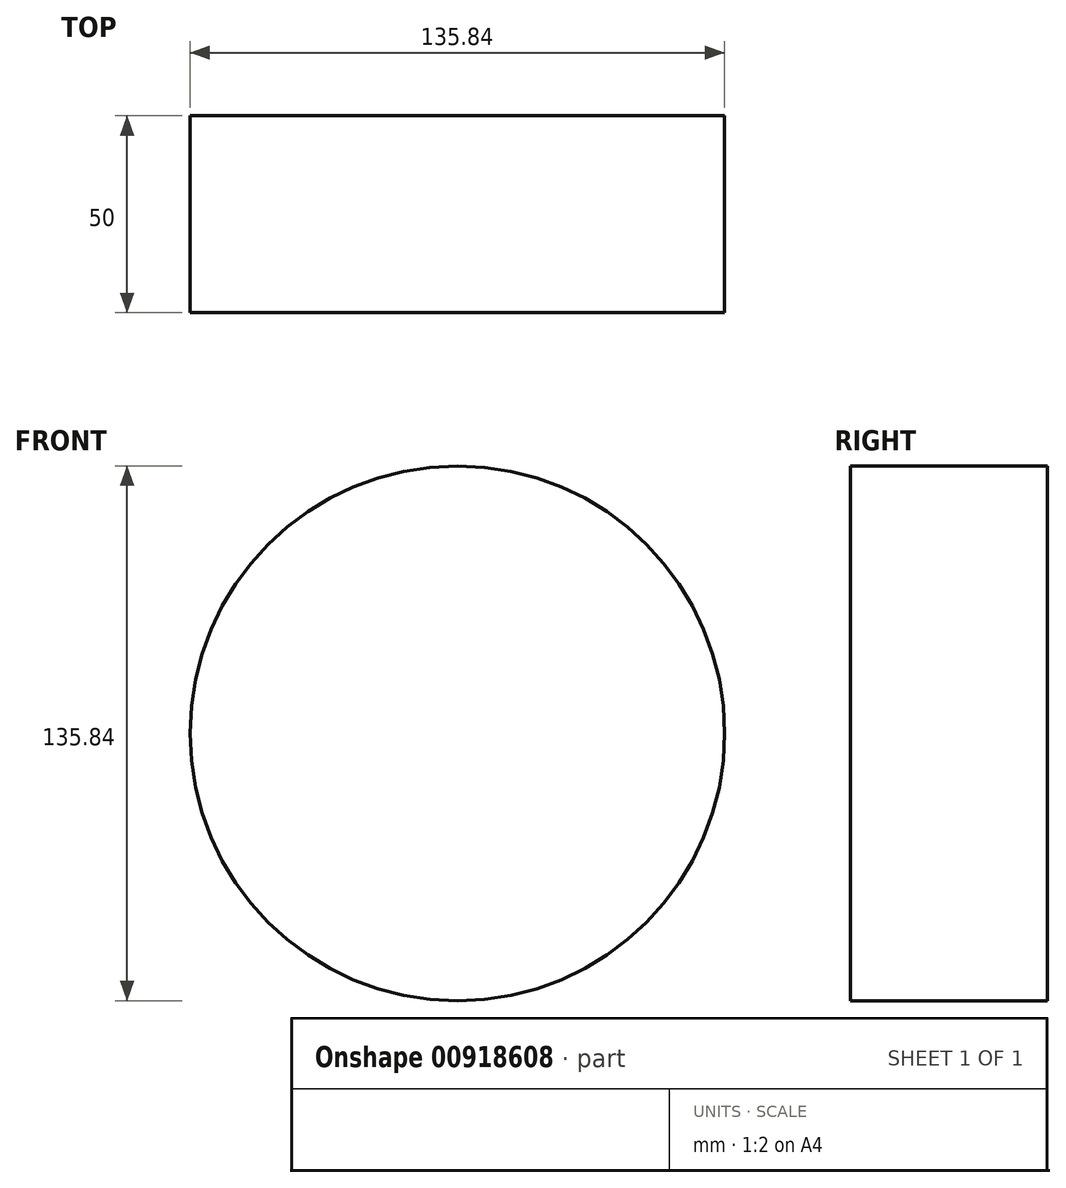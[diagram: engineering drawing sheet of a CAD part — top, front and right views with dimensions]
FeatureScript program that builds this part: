
annotation { "Feature Type Name" : "Feature", "Feature Type Description" : "" }
export const myFeature = defineFeature(function(context is Context, id is Id, definition is map)
    precondition{}
    {
        {
            var Q0;
            Q0=qCreatedBy(makeId("Front.planeOp"),FACE);
            var sketch = newSketch(context, id + "F0", { "sketchPlane" : qUnion([Q0])});
            skCircle(sketch, "E0", {"center": v(0, 0) * mm, "radius": 67.92 * mm});
            skSolve(sketch);
        }
        {
            var Q0;
            Q0 = qSketchRegion(id + "F0", true);
            extrude(context, id + "F1", {"entities" : qUnion([Q0]), "depth" : 25 * mm, "offsetDistance" : 25 * mm, "hasSecondDirection" : true, "secondDirectionOppositeDirection" : true, "secondDirectionDepth" : 25 * mm});
        }
    });
